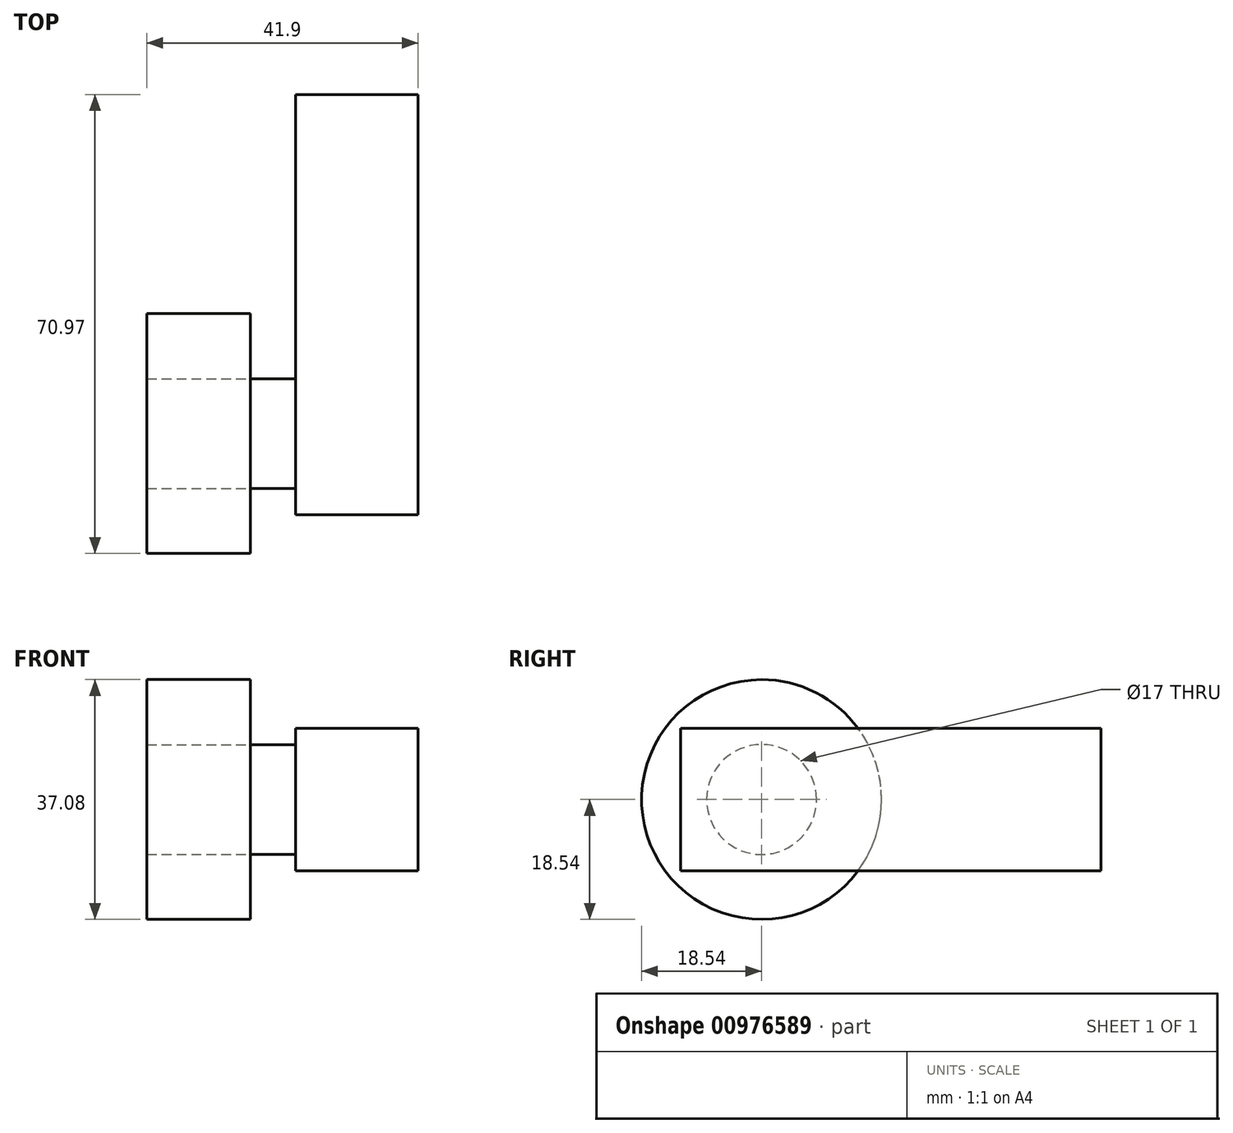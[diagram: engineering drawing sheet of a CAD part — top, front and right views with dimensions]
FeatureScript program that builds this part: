
annotation { "Feature Type Name" : "Feature", "Feature Type Description" : "" }
export const myFeature = defineFeature(function(context is Context, id is Id, definition is map)
    precondition{}
    {
        {
            var Q0;
            Q0=qCreatedBy(makeId("Top.planeOp"),FACE);
            var sketch = newSketch(context, id + "F0", { "sketchPlane" : qUnion([Q0])});
            skLineSegment(sketch, "E0.bottom", {"start": v(-11.97, 42.12) * mm, "end": v(6.93, 42.12) * mm});
            skLineSegment(sketch, "E0.top", {"start": v(-11.97, -22.86) * mm, "end": v(6.93, -22.86) * mm});
            skLineSegment(sketch, "E0.left", {"start": v(-11.97, 42.12) * mm, "end": v(-11.97, -22.86) * mm});
            skLineSegment(sketch, "E0.right", {"start": v(6.93, 42.12) * mm, "end": v(6.93, -22.86) * mm});
            skSolve(sketch);
        }
        {
            var Q0;
            Q0=makeQuery(id+"F0.imprint","IMPRINT",FACE,{"disambiguationData":[TD([[makeQuery(id+"F0.imprint","IMPRINT",EDGE,{"derivedFrom":sQuery(id+"F0.wireOp",EDGE,"E0.bottom")}),-1.0]])]});
            extrude(context, id + "F1", {"entities" : qUnion([Q0]), "depth" : 22 * mm, "offsetDistance" : 25 * mm});
        }
        {
            var Q0;
            Q0=makeQuery(id+"F1.opExtrude","SWEPT_FACE",FACE,{"disambiguationData":[OSD([sQuery(id+"F0.wireOp",EDGE,"E0.left")])]});
            var sketch = newSketch(context, id + "F2", { "sketchPlane" : qUnion([Q0])});
            skCircle(sketch, "E1", {"center": v(10.31, 11) * mm, "radius": 8.5 * mm});
            skSolve(sketch);
        }
        {
            var Q0;
            Q0=makeQuery(id+"F2.imprint","IMPRINT",FACE,{"disambiguationData":[TD([[makeQuery(id+"F2.imprint","IMPRINT",EDGE,{"derivedFrom":sQuery(id+"F2.wireOp",EDGE,"E1")}),1.0]])]});
            extrude(context, id + "F3", {"entities" : qUnion([Q0]), "operationType" : NewBodyOperationType.ADD, "depth" : 7 * mm, "offsetDistance" : 25 * mm});
        }
        {
            var Q0;
            Q0=makeQuery(id+"F3.opExtrude","CAP_FACE",FACE,{"disambiguationData":[OSD([sQuery(id+"F2.wireOp",EDGE,"E1")])],"isStart":false});
            var sketch = newSketch(context, id + "F4", { "sketchPlane" : qUnion([Q0])});
            skCircle(sketch, "E2", {"center": v(10.31, 11) * mm, "radius": 18.54 * mm});
            skSolve(sketch);
        }
        {
            var Q0;
            Q0=makeQuery(id+"F4.imprint","IMPRINT",FACE,{"disambiguationData":[TD([[makeQuery(id+"F4.imprint","IMPRINT",EDGE,{"derivedFrom":sQuery(id+"F4.wireOp",EDGE,"E2")}),1.0]])]});
            extrude(context, id + "F5", {"entities" : qUnion([Q0]), "depth" : 16 * mm, "offsetDistance" : 25 * mm});
        }
    });
